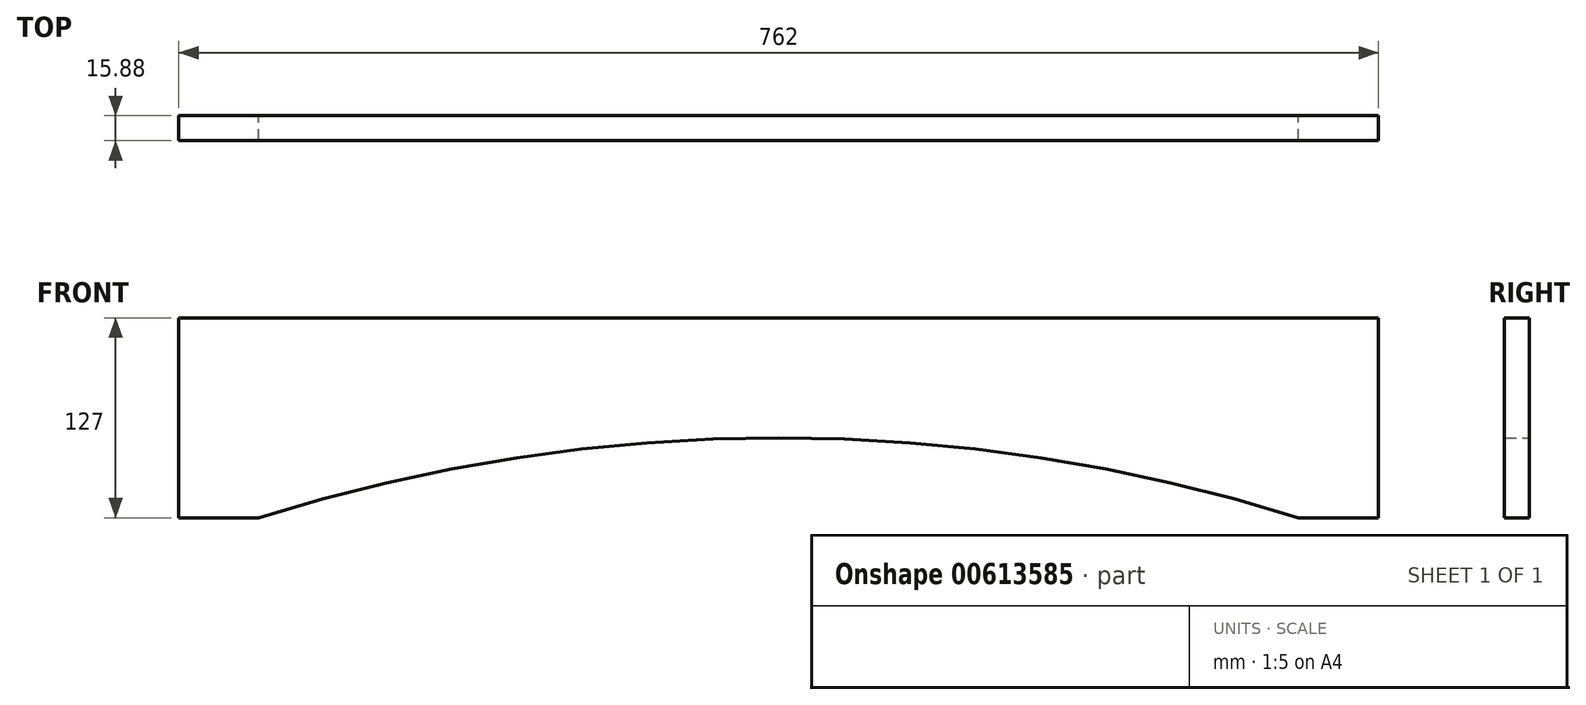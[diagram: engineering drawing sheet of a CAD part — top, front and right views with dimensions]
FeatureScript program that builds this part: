
annotation { "Feature Type Name" : "Feature", "Feature Type Description" : "" }
export const myFeature = defineFeature(function(context is Context, id is Id, definition is map)
    precondition{}
    {
        {
            var Q0;
            Q0=qCreatedBy(makeId("Front.planeOp"),FACE);
            var sketch = newSketch(context, id + "F0", { "sketchPlane" : qUnion([Q0])});
            skLineSegment(sketch, "E0", {"start": v(-71.57, 76.2) * mm, "end": v(690.43, 76.2) * mm});
            skLineSegment(sketch, "E1", {"start": v(690.43, 76.2) * mm, "end": v(690.43, -50.8) * mm});
            skLineSegment(sketch, "E2", {"start": v(-71.57, 76.2) * mm, "end": v(-71.57, -50.8) * mm});
            skLineSegment(sketch, "E3", {"start": v(-71.57, -50.8) * mm, "end": v(-20.77, -50.8) * mm});
            skLineSegment(sketch, "E4", {"start": v(690.43, -50.8) * mm, "end": v(639.63, -50.8) * mm});
            skArc(sketch, "E5", {"start": v(639.63, -50.8) * mm, "mid": v(309.43, 0) * mm, "end": v(-20.77, -50.8) * mm});
            skPoint(sketch, "E6.end.orphan", {"position": v(309.43, 0) * mm});
            skPoint(sketch, "E6.start.orphan", {"position": v(309.43, 76.2) * mm});
            skSolve(sketch);
        }
        {
            var Q0;
            Q0 = qSketchRegion(id + "F0", true);
            extrude(context, id + "F1", {"entities" : qUnion([Q0]), "depth" : 15.88 * mm, "offsetDistance" : 25.4 * mm});
        }
    });
